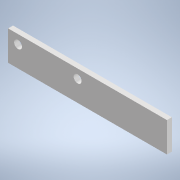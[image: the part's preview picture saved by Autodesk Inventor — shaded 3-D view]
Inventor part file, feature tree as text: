
AUTODESK INVENTOR PART (.ipt)
format: ipt  version: 2022 (Build 260153000, 153)  size: 101,376 bytes
history: native  units: mm
features: reference x2, other x2, extrude x1, sketch x1
ambient origin geometry x8: Origin, YZ Plane, XZ Plane, XY Plane, X Axis, Y Axis, Z Axis, Center Point
bodies: Solid1 (feature_tree)
feature tree (6):
  extrude  "Extrusion1"  Depth=2.5mm
  sketch  "Sketch1"  dims[d0=4.0mm d1=4.0mm d2=15.0mm d3=80.0mm d4=4.5mm d5=5.0mm d6=2.5mm d7=0.0mm]
  reference  "Reference1"
  reference  "Reference2"
  other  "Final_Reduccion.iam"
  other  "Base_proyecto:1"
